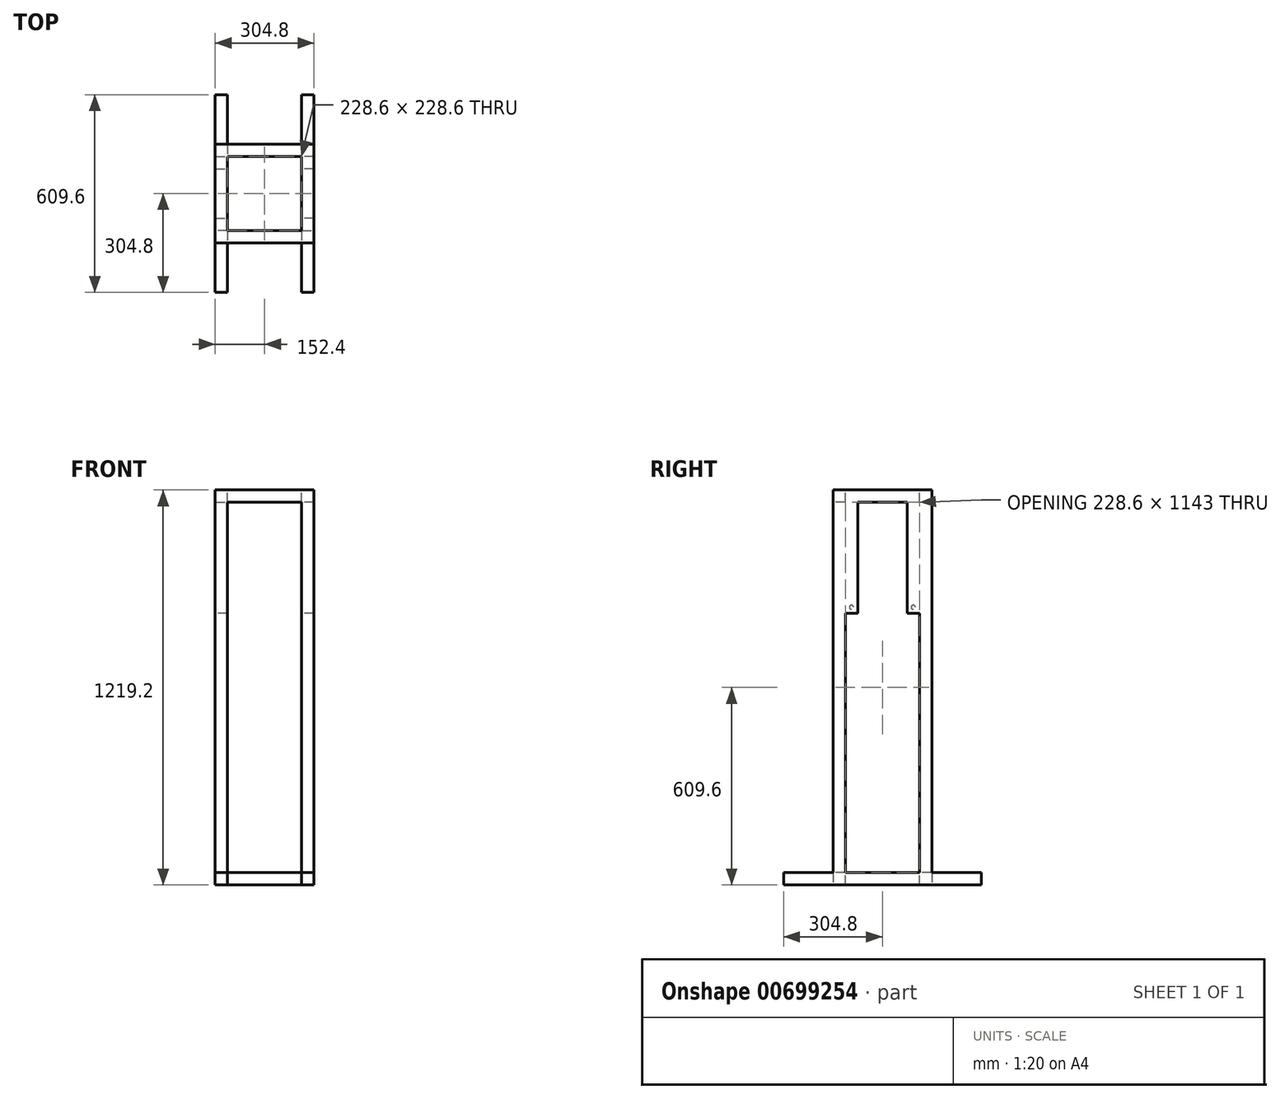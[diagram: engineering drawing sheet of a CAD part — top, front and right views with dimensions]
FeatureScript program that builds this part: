
annotation { "Feature Type Name" : "Feature", "Feature Type Description" : "" }
export const myFeature = defineFeature(function(context is Context, id is Id, definition is map)
    precondition{}
    {
        {
            var Q0;
            Q0=qCreatedBy(makeId("Top.planeOp"),FACE);
            var sketch = newSketch(context, id + "F0", { "sketchPlane" : qUnion([Q0])});
            skLineSegment(sketch, "E0.bottom", {"start": v(152.4, -152.4) * mm, "end": v(-152.4, -152.4) * mm});
            skLineSegment(sketch, "E0.top", {"start": v(152.4, 152.4) * mm, "end": v(-152.4, 152.4) * mm});
            skLineSegment(sketch, "E0.left", {"start": v(152.4, -152.4) * mm, "end": v(152.4, 152.4) * mm});
            skLineSegment(sketch, "E0.right", {"start": v(-152.4, -152.4) * mm, "end": v(-152.4, 152.4) * mm});
            skPoint(sketch, "E0.middle", {"position": v(0, 0) * mm});
            skSolve(sketch);
        }
        {
            var Q0;
            Q0=makeQuery(id+"F0.imprint","IMPRINT",FACE,{"disambiguationData":[TD([[makeQuery(id+"F0.imprint","IMPRINT",EDGE,{"derivedFrom":sQuery(id+"F0.wireOp",EDGE,"E0.bottom")}),-1.0]])]});
            extrude(context, id + "F1", {"entities" : qUnion([Q0]), "oppositeDirection" : true, "depth" : 38.1 * mm, "offsetDistance" : 25.4 * mm});
        }
        {
            var Q0;
            Q0=makeQuery(id+"F1.opExtrude","CAP_FACE",FACE,{"disambiguationData":[OSD([sQuery(id+"F0.wireOp",EDGE,"E0.bottom"),sQuery(id+"F0.wireOp",EDGE,"E0.top"),sQuery(id+"F0.wireOp",EDGE,"E0.left"),sQuery(id+"F0.wireOp",EDGE,"E0.right")])],"isStart":true});
            var sketch = newSketch(context, id + "F2", { "sketchPlane" : qUnion([Q0])});
            skLineSegment(sketch, "E1.bottom", {"start": v(114.3, -114.3) * mm, "end": v(-114.3, -114.3) * mm});
            skLineSegment(sketch, "E1.top", {"start": v(114.3, 114.3) * mm, "end": v(-114.3, 114.3) * mm});
            skLineSegment(sketch, "E1.left", {"start": v(114.3, -114.3) * mm, "end": v(114.3, 114.3) * mm});
            skLineSegment(sketch, "E1.right", {"start": v(-114.3, -114.3) * mm, "end": v(-114.3, 114.3) * mm});
            skPoint(sketch, "E1.middle", {"position": v(0, 0) * mm});
            skSolve(sketch);
        }
        {
            var Q0;
            Q0 = qSketchRegion(id + "F2", true);
            extrude(context, id + "F3", {"entities" : qUnion([Q0]), "operationType" : NewBodyOperationType.REMOVE, "oppositeDirection" : true, "depth" : 38.1 * mm, "offsetDistance" : 25.4 * mm});
        }
        {
            var Q0;
            Q0=makeQuery(id+"F1.opExtrude","CAP_FACE",FACE,{"disambiguationData":[OSD([sQuery(id+"F0.wireOp",EDGE,"E0.bottom"),sQuery(id+"F0.wireOp",EDGE,"E0.top"),sQuery(id+"F0.wireOp",EDGE,"E0.left"),sQuery(id+"F0.wireOp",EDGE,"E0.right")])],"isStart":true});
            var sketch = newSketch(context, id + "F4", { "sketchPlane" : qUnion([Q0])});
            skLineSegment(sketch, "E2.bottom", {"start": v(-152.4, 152.4) * mm, "end": v(-114.3, 152.4) * mm});
            skLineSegment(sketch, "E2.top", {"start": v(-152.4, 114.3) * mm, "end": v(-114.3, 114.3) * mm});
            skLineSegment(sketch, "E2.left", {"start": v(-152.4, 152.4) * mm, "end": v(-152.4, 114.3) * mm});
            skLineSegment(sketch, "E2.right", {"start": v(-114.3, 152.4) * mm, "end": v(-114.3, 114.3) * mm});
            skLineSegment(sketch, "E3.bottom", {"start": v(152.4, 152.4) * mm, "end": v(114.3, 152.4) * mm});
            skLineSegment(sketch, "E3.top", {"start": v(152.4, 114.3) * mm, "end": v(114.3, 114.3) * mm});
            skLineSegment(sketch, "E3.left", {"start": v(152.4, 152.4) * mm, "end": v(152.4, 114.3) * mm});
            skLineSegment(sketch, "E3.right", {"start": v(114.3, 152.4) * mm, "end": v(114.3, 114.3) * mm});
            skLineSegment(sketch, "E4.bottom", {"start": v(114.3, -114.3) * mm, "end": v(152.4, -114.3) * mm});
            skLineSegment(sketch, "E4.top", {"start": v(114.3, -152.4) * mm, "end": v(152.4, -152.4) * mm});
            skLineSegment(sketch, "E4.left", {"start": v(114.3, -114.3) * mm, "end": v(114.3, -152.4) * mm});
            skLineSegment(sketch, "E4.right", {"start": v(152.4, -114.3) * mm, "end": v(152.4, -152.4) * mm});
            skLineSegment(sketch, "E5.bottom", {"start": v(-114.3, -114.3) * mm, "end": v(-152.4, -114.3) * mm});
            skLineSegment(sketch, "E5.top", {"start": v(-114.3, -152.4) * mm, "end": v(-152.4, -152.4) * mm});
            skLineSegment(sketch, "E5.left", {"start": v(-114.3, -114.3) * mm, "end": v(-114.3, -152.4) * mm});
            skLineSegment(sketch, "E5.right", {"start": v(-152.4, -114.3) * mm, "end": v(-152.4, -152.4) * mm});
            skSolve(sketch);
        }
        {
            var Q0;
            Q0 = qSketchRegion(id + "F4", true);
            extrude(context, id + "F5", {"entities" : qUnion([Q0]), "operationType" : NewBodyOperationType.ADD, "depth" : 1143 * mm, "offsetDistance" : 25.4 * mm});
        }
        {
            var Q0;
            Q0=makeQuery(id+"F5.opExtrude","CAP_FACE",FACE,{"disambiguationData":[OSD([sQuery(id+"F4.wireOp",EDGE,"E2.bottom"),sQuery(id+"F4.wireOp",EDGE,"E2.top"),sQuery(id+"F4.wireOp",EDGE,"E2.left"),sQuery(id+"F4.wireOp",EDGE,"E2.right")])],"isStart":false});
            var sketch = newSketch(context, id + "F6", { "sketchPlane" : qUnion([Q0])});
            skLineSegment(sketch, "E6.bottom", {"start": v(-152.4, 152.4) * mm, "end": v(152.4, 152.4) * mm});
            skLineSegment(sketch, "E6.top", {"start": v(-152.4, -152.4) * mm, "end": v(152.4, -152.4) * mm});
            skLineSegment(sketch, "E6.left", {"start": v(-152.4, 152.4) * mm, "end": v(-152.4, -152.4) * mm});
            skLineSegment(sketch, "E6.right", {"start": v(152.4, 152.4) * mm, "end": v(152.4, -152.4) * mm});
            skSolve(sketch);
        }
        {
            var Q0;
            Q0 = qSketchRegion(id + "F6", true);
            extrude(context, id + "F7", {"entities" : qUnion([Q0]), "operationType" : NewBodyOperationType.ADD, "depth" : 38.1 * mm, "offsetDistance" : 25.4 * mm});
        }
        {
            var Q0;
            Q0=makeQuery(id+"F7.opExtrude","CAP_FACE",FACE,{"disambiguationData":[OSD([sQuery(id+"F6.wireOp",EDGE,"E6.bottom"),sQuery(id+"F6.wireOp",EDGE,"E6.top"),sQuery(id+"F6.wireOp",EDGE,"E6.left"),sQuery(id+"F6.wireOp",EDGE,"E6.right")])],"isStart":false});
            var sketch = newSketch(context, id + "F8", { "sketchPlane" : qUnion([Q0])});
            skLineSegment(sketch, "E7.bottom", {"start": v(114.3, -114.3) * mm, "end": v(-114.3, -114.3) * mm});
            skLineSegment(sketch, "E7.top", {"start": v(114.3, 114.3) * mm, "end": v(-114.3, 114.3) * mm});
            skLineSegment(sketch, "E7.left", {"start": v(114.3, -114.3) * mm, "end": v(114.3, 114.3) * mm});
            skLineSegment(sketch, "E7.right", {"start": v(-114.3, -114.3) * mm, "end": v(-114.3, 114.3) * mm});
            skPoint(sketch, "E7.middle", {"position": v(0, 0) * mm});
            skSolve(sketch);
        }
        {
            var Q0;
            Q0=makeQuery(id+"F8.imprint","IMPRINT",FACE,{"disambiguationData":[TD([[makeQuery(id+"F8.imprint","IMPRINT",EDGE,{"derivedFrom":sQuery(id+"F8.wireOp",EDGE,"E7.bottom")}),-1.0]])]});
            extrude(context, id + "F9", {"entities" : qUnion([Q0]), "operationType" : NewBodyOperationType.REMOVE, "oppositeDirection" : true, "depth" : 38.1 * mm, "offsetDistance" : 25.4 * mm});
        }
        {
            var Q0;
            {var subQ0=sQuery(id+"F6.wireOp",EDGE,"E6.right");var subQ1=makeQuery(id+"F7.opExtrude","CAP_FACE",FACE,{"disambiguationData":[OSD([sQuery(id+"F6.wireOp",EDGE,"E6.bottom"),sQuery(id+"F6.wireOp",EDGE,"E6.top"),sQuery(id+"F6.wireOp",EDGE,"E6.left"),subQ0])],"isStart":true});Q0=makeQuery(id+"F9.boolean.opBoolean","SPLIT",FACE,{"disambiguationData":[TD([makeQuery(id+"F1.opExtrude","SWEPT_FACE",FACE,{"disambiguationData":[OSD([sQuery(id+"F0.wireOp",EDGE,"E0.left")])]})])],"derivedFrom":subQ1});}
            var sketch = newSketch(context, id + "F10", { "sketchPlane" : qUnion([Q0])});
            skLineSegment(sketch, "E8.bottom", {"start": v(152.4, 114.3) * mm, "end": v(114.3, 114.3) * mm});
            skLineSegment(sketch, "E8.top", {"start": v(152.4, 76.2) * mm, "end": v(114.3, 76.2) * mm});
            skLineSegment(sketch, "E8.left", {"start": v(152.4, 114.3) * mm, "end": v(152.4, 76.2) * mm});
            skLineSegment(sketch, "E8.right", {"start": v(114.3, 114.3) * mm, "end": v(114.3, 76.2) * mm});
            skLineSegment(sketch, "E9.bottom", {"start": v(152.4, -114.3) * mm, "end": v(114.3, -114.3) * mm});
            skLineSegment(sketch, "E9.top", {"start": v(152.4, -76.2) * mm, "end": v(114.3, -76.2) * mm});
            skLineSegment(sketch, "E9.left", {"start": v(152.4, -114.3) * mm, "end": v(152.4, -76.2) * mm});
            skLineSegment(sketch, "E9.right", {"start": v(114.3, -114.3) * mm, "end": v(114.3, -76.2) * mm});
            skSolve(sketch);
        }
        {
            var Q0;
            Q0 = qSketchRegion(id + "F10", true);
            extrude(context, id + "F11", {"entities" : qUnion([Q0]), "operationType" : NewBodyOperationType.ADD, "depth" : 342.9 * mm, "offsetDistance" : 25.4 * mm});
        }
        {
            var Q0;
            {var subQ0=sQuery(id+"F6.wireOp",EDGE,"E6.left");var subQ1=makeQuery(id+"F7.opExtrude","CAP_FACE",FACE,{"disambiguationData":[OSD([sQuery(id+"F6.wireOp",EDGE,"E6.bottom"),sQuery(id+"F6.wireOp",EDGE,"E6.top"),subQ0,sQuery(id+"F6.wireOp",EDGE,"E6.right")])],"isStart":true});Q0=makeQuery(id+"F9.boolean.opBoolean","SPLIT",FACE,{"disambiguationData":[TD([makeQuery(id+"F1.opExtrude","SWEPT_FACE",FACE,{"disambiguationData":[OSD([sQuery(id+"F0.wireOp",EDGE,"E0.right")])]})])],"derivedFrom":subQ1});}
            var sketch = newSketch(context, id + "F12", { "sketchPlane" : qUnion([Q0])});
            skLineSegment(sketch, "E10.bottom", {"start": v(-152.4, -114.3) * mm, "end": v(-114.3, -114.3) * mm});
            skLineSegment(sketch, "E10.top", {"start": v(-152.4, -76.2) * mm, "end": v(-114.3, -76.2) * mm});
            skLineSegment(sketch, "E10.left", {"start": v(-152.4, -114.3) * mm, "end": v(-152.4, -76.2) * mm});
            skLineSegment(sketch, "E10.right", {"start": v(-114.3, -114.3) * mm, "end": v(-114.3, -76.2) * mm});
            skLineSegment(sketch, "E11.bottom", {"start": v(-152.4, 114.3) * mm, "end": v(-114.3, 114.3) * mm});
            skLineSegment(sketch, "E11.top", {"start": v(-152.4, 76.2) * mm, "end": v(-114.3, 76.2) * mm});
            skLineSegment(sketch, "E11.left", {"start": v(-152.4, 114.3) * mm, "end": v(-152.4, 76.2) * mm});
            skLineSegment(sketch, "E11.right", {"start": v(-114.3, 114.3) * mm, "end": v(-114.3, 76.2) * mm});
            skSolve(sketch);
        }
        {
            var Q0;
            Q0 = qSketchRegion(id + "F12", true);
            extrude(context, id + "F13", {"entities" : qUnion([Q0]), "operationType" : NewBodyOperationType.ADD, "depth" : 342.9 * mm, "offsetDistance" : 25.4 * mm});
        }
        {
            var Q0;
            Q0=makeQuery(id+"F13.boolean.opBoolean","MERGE",FACE,{"derivedFrom":[makeQuery(id+"F5.opExtrude","SWEPT_FACE",FACE,{"disambiguationData":[OSD([sQuery(id+"F4.wireOp",EDGE,"E2.right")])]}),makeQuery(id+"F5.opExtrude","SWEPT_FACE",FACE,{"disambiguationData":[OSD([sQuery(id+"F4.wireOp",EDGE,"E5.left")])]}),makeQuery(id+"F9.boolean.opBoolean","COPY",FACE,{"derivedFrom":makeQuery(id+"F9.opExtrude","SWEPT_FACE",FACE,{"disambiguationData":[OSD([sQuery(id+"F8.wireOp",EDGE,"E7.right")])]})}),makeQuery(id+"F13.opExtrude","SWEPT_FACE",FACE,{"disambiguationData":[OSD([sQuery(id+"F12.wireOp",EDGE,"E10.right")])]}),makeQuery(id+"F13.opExtrude","SWEPT_FACE",FACE,{"disambiguationData":[OSD([sQuery(id+"F12.wireOp",EDGE,"E11.right")])]})]});
            var sketch = newSketch(context, id + "F14", { "sketchPlane" : qUnion([Q0])});
            skLineSegment(sketch, "E12.bottom", {"start": v(-76.2, 800.1) * mm, "end": v(-114.3, 800.1) * mm});
            skLineSegment(sketch, "E12.top", {"start": v(-76.2, 838.2) * mm, "end": v(-114.3, 838.2) * mm});
            skLineSegment(sketch, "E12.left", {"start": v(-76.2, 800.1) * mm, "end": v(-76.2, 838.2) * mm});
            skLineSegment(sketch, "E12.right", {"start": v(-114.3, 800.1) * mm, "end": v(-114.3, 838.2) * mm});
            skLineSegment(sketch, "E13.bottom", {"start": v(114.3, 800.1) * mm, "end": v(76.2, 800.1) * mm});
            skLineSegment(sketch, "E13.top", {"start": v(114.3, 838.2) * mm, "end": v(76.2, 838.2) * mm});
            skLineSegment(sketch, "E13.left", {"start": v(114.3, 800.1) * mm, "end": v(114.3, 838.2) * mm});
            skLineSegment(sketch, "E13.right", {"start": v(76.2, 800.1) * mm, "end": v(76.2, 838.2) * mm});
            skCircle(sketch, "E14", {"center": v(-95.25, 819.15) * mm, "radius": 6.35 * mm});
            skCircle(sketch, "E15", {"center": v(95.25, 819.15) * mm, "radius": 6.35 * mm});
            skSolve(sketch);
        }
        {
            var Q0;
            Q0=makeQuery(id+"F11.boolean.opBoolean","MERGE",FACE,{"derivedFrom":[makeQuery(id+"F5.opExtrude","SWEPT_FACE",FACE,{"disambiguationData":[OSD([sQuery(id+"F4.wireOp",EDGE,"E3.right")])]}),makeQuery(id+"F5.opExtrude","SWEPT_FACE",FACE,{"disambiguationData":[OSD([sQuery(id+"F4.wireOp",EDGE,"E4.left")])]}),makeQuery(id+"F9.boolean.opBoolean","COPY",FACE,{"derivedFrom":makeQuery(id+"F9.opExtrude","SWEPT_FACE",FACE,{"disambiguationData":[OSD([sQuery(id+"F8.wireOp",EDGE,"E7.left")])]})}),makeQuery(id+"F11.opExtrude","SWEPT_FACE",FACE,{"disambiguationData":[OSD([sQuery(id+"F10.wireOp",EDGE,"E8.right")])]}),makeQuery(id+"F11.opExtrude","SWEPT_FACE",FACE,{"disambiguationData":[OSD([sQuery(id+"F10.wireOp",EDGE,"E9.right")])]})]});
            var sketch = newSketch(context, id + "F15", { "sketchPlane" : qUnion([Q0])});
            skLineSegment(sketch, "E16.bottom", {"start": v(-114.3, 800.1) * mm, "end": v(-76.2, 800.1) * mm});
            skLineSegment(sketch, "E16.top", {"start": v(-114.3, 838.2) * mm, "end": v(-76.2, 838.2) * mm});
            skLineSegment(sketch, "E16.left", {"start": v(-114.3, 800.1) * mm, "end": v(-114.3, 838.2) * mm});
            skLineSegment(sketch, "E16.right", {"start": v(-76.2, 800.1) * mm, "end": v(-76.2, 838.2) * mm});
            skLineSegment(sketch, "E17.bottom", {"start": v(114.3, 800.1) * mm, "end": v(76.2, 800.1) * mm});
            skLineSegment(sketch, "E17.top", {"start": v(114.3, 838.2) * mm, "end": v(76.2, 838.2) * mm});
            skLineSegment(sketch, "E17.left", {"start": v(114.3, 800.1) * mm, "end": v(114.3, 838.2) * mm});
            skLineSegment(sketch, "E17.right", {"start": v(76.2, 800.1) * mm, "end": v(76.2, 838.2) * mm});
            skCircle(sketch, "E18", {"center": v(-95.25, 819.15) * mm, "radius": 6.35 * mm});
            skPoint(sketch, "E18.centerSnap0", {"position": v(-76.2, 819.15) * mm});
            skPoint(sketch, "E18.centerSnap1", {"position": v(-95.25, 800.1) * mm});
            skCircle(sketch, "E19", {"center": v(95.25, 819.15) * mm, "radius": 6.35 * mm});
            skPoint(sketch, "E19.centerSnap0", {"position": v(95.25, 800.1) * mm});
            skPoint(sketch, "E19.centerSnap1", {"position": v(76.2, 819.15) * mm});
            skSolve(sketch);
        }
        {
            var Q0;
            Q0=makeQuery(id+"F14.imprint","IMPRINT",FACE,{"disambiguationData":[TD([[makeQuery(id+"F14.imprint","IMPRINT",EDGE,{"derivedFrom":sQuery(id+"F14.wireOp",EDGE,"E15")}),1.0]])]});
            var Q1;
            Q1=makeQuery(id+"F14.imprint","IMPRINT",FACE,{"disambiguationData":[TD([[makeQuery(id+"F14.imprint","IMPRINT",EDGE,{"derivedFrom":sQuery(id+"F14.wireOp",EDGE,"E14")}),1.0]])]});
            extrude(context, id + "F16", {"entities" : qUnion([Q0, Q1]), "operationType" : NewBodyOperationType.REMOVE, "oppositeDirection" : true, "depth" : 0.25 * mm, "offsetDistance" : 25.4 * mm});
        }
        {
            var Q0;
            Q0=makeQuery(id+"F15.imprint","IMPRINT",FACE,{"disambiguationData":[TD([[makeQuery(id+"F15.imprint","IMPRINT",EDGE,{"derivedFrom":sQuery(id+"F15.wireOp",EDGE,"E18")}),1.0]])]});
            var Q1;
            Q1=makeQuery(id+"F15.imprint","IMPRINT",FACE,{"disambiguationData":[TD([[makeQuery(id+"F15.imprint","IMPRINT",EDGE,{"derivedFrom":sQuery(id+"F15.wireOp",EDGE,"E19")}),1.0]])]});
            extrude(context, id + "F17", {"entities" : qUnion([Q0, Q1]), "operationType" : NewBodyOperationType.REMOVE, "oppositeDirection" : true, "depth" : 0.25 * mm, "offsetDistance" : 25.4 * mm});
        }
        {
            var Q0;
            Q0=qCreatedBy(makeId("Front.planeOp"),FACE);
            var sketch = newSketch(context, id + "F18", { "sketchPlane" : qUnion([Q0])});
            skLineSegment(sketch, "E20.bottom", {"start": v(152.4, 0) * mm, "end": v(114.3, 0) * mm});
            skLineSegment(sketch, "E20.top", {"start": v(152.4, -38.1) * mm, "end": v(114.3, -38.1) * mm});
            skLineSegment(sketch, "E20.left", {"start": v(152.4, 0) * mm, "end": v(152.4, -38.1) * mm});
            skLineSegment(sketch, "E20.right", {"start": v(114.3, 0) * mm, "end": v(114.3, -38.1) * mm});
            skLineSegment(sketch, "E21.bottom", {"start": v(-152.4, 0) * mm, "end": v(-114.3, 0) * mm});
            skLineSegment(sketch, "E21.top", {"start": v(-152.4, -38.1) * mm, "end": v(-114.3, -38.1) * mm});
            skLineSegment(sketch, "E21.left", {"start": v(-152.4, 0) * mm, "end": v(-152.4, -38.1) * mm});
            skLineSegment(sketch, "E21.right", {"start": v(-114.3, 0) * mm, "end": v(-114.3, -38.1) * mm});
            skSolve(sketch);
        }
        {
            var Q0;
            Q0 = qSketchRegion(id + "F18", true);
            extrude(context, id + "F19", {"entities" : qUnion([Q0]), "operationType" : NewBodyOperationType.ADD, "endBound" : BoundingType.SYMMETRIC, "depth" : 609.6 * mm, "offsetDistance" : 25.4 * mm});
        }
    });
